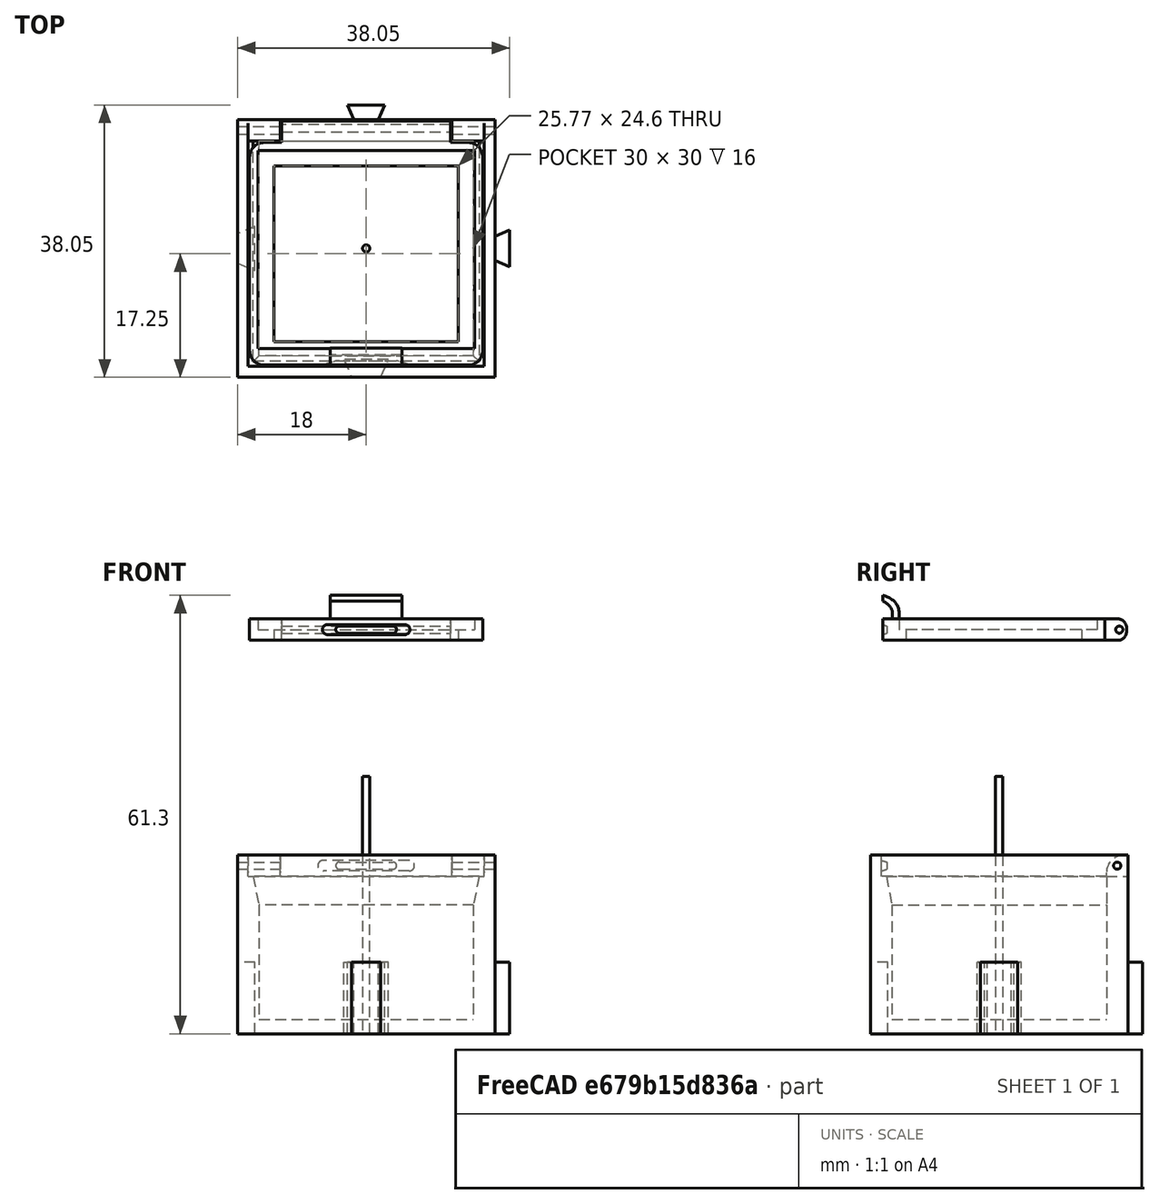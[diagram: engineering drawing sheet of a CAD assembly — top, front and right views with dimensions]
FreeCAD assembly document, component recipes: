
FREECAD ASSEMBLY — COMPONENT RECIPES ("smd_smt_modular_boxes")

This assembly document has 3 components, labeled P0..P2 below (a component is one placed body or linked part). 3 of them carry a construction recipe — the FreeCAD feature program that regenerates the part from scratch, quoted from this document or its linked companion documents; the rest are supplied as boundary geometry only. No exploded tour is included for this assembly.
COMPONENT P0 — recipe-attached ("box", modeled in this document).
Construction recipe (the document's own serialized feature program — sketch geometry with constraints, then the solid features built on it; lengths are millimeters unless a unit is written):

FEATURE [PartDesign::CoordinateSystem] LCS_0
  AttacherType = Attacher::AttachEngine3D
  MapMode = 2
  Support = -> [X_Axis001]
FEATURE [PartDesign::Plane] DatumPlane
  Length = 60
  MapMode = 5
  ResizeMode = 0
  Support = -> [XY_Plane001]
  Width = 60
FEATURE [Sketcher::SketchObject] Sketch  label="baseExternal"
  MapMode = 5
  Support = -> [DatumPlane]
  expr: Constraints[8] = Spreadsheet.lenght + Spreadsheet.wallWidth * 2
  expr: Constraints[9] = Spreadsheet.width + Spreadsheet.wallWidth * 2
  sketch-geometry (4):
    g0: LineSegment StartX=-18 StartY=18 StartZ=0 EndX=18 EndY=18 EndZ=0
    g1: LineSegment StartX=18 StartY=18 StartZ=0 EndX=18 EndY=-18 EndZ=0
    g2: LineSegment StartX=18 StartY=-18 StartZ=0 EndX=-18 EndY=-18 EndZ=0
    g3: LineSegment StartX=-18 StartY=-18 StartZ=0 EndX=-18 EndY=18 EndZ=0
  constraints (10):
    c: Coincident(g0,g1)
    c: Coincident(g1,g2)
    c: Coincident(g2,g3)
    c: Coincident(g3,g0)
    c: Horizontal(g2)
    c: Vertical(g3)
    c: Symmetric(g0,g0,g-2)
    c: Symmetric(g0,g1,g-1)
    c: DistanceX(g0,g0) = 36
    c: DistanceY(g1,g0) = 36
FEATURE [PartDesign::Pad] Pad
  Length = 22
  Length2 = 100
  Profile = -> Sketch
  Type = 0
  expr: Length = Spreadsheet.hight + Spreadsheet.buttonPad
FEATURE [PartDesign::ShapeBinder] ShapeBinder  label="baseExternalBinder"
  Support = -> [Sketch]
  TraceSupport = false
FEATURE [Sketcher::SketchObject] Sketch001  label="outsideDovetail"
  ExternalGeometry = -> [ShapeBinder]
  MapMode = 5
  Support = -> [DatumPlane]
  expr: Constraints[7] = Spreadsheet.wallWidth * 0.75 - Spreadsheet.clearance
  expr: Constraints[8] = Spreadsheet.wallWidth * 1.8 - Spreadsheet.clearance
  expr: Constraints[9] = Spreadsheet.wallWidth * 1.2 - Spreadsheet.clearance
  expr: Constraints[19] = Spreadsheet.wallWidth * 0.75 - Spreadsheet.clearance
  sketch-geometry (8):
    g0: LineSegment StartX=-1.7 StartY=18 StartZ=0 EndX=1.7 EndY=18 EndZ=0
    g1: LineSegment StartX=1.7 StartY=18 StartZ=0 EndX=2.6 EndY=20.05 EndZ=0
    g2: LineSegment StartX=2.6 StartY=20.05 StartZ=0 EndX=-2.6 EndY=20.05 EndZ=0
    g3: LineSegment StartX=-2.6 StartY=20.05 StartZ=0 EndX=-1.7 EndY=18 EndZ=0
    g4: LineSegment StartX=18 StartY=1.7 StartZ=0 EndX=18 EndY=-1.7 EndZ=0
    g5: LineSegment StartX=18 StartY=-1.7 StartZ=0 EndX=20.05 EndY=-2.6 EndZ=0
    g6: LineSegment StartX=20.05 StartY=-2.6 StartZ=0 EndX=20.05 EndY=2.6 EndZ=0
    g7: LineSegment StartX=20.05 StartY=2.6 StartZ=0 EndX=18 EndY=1.7 EndZ=0
  constraints (20):
    c: PointOnObject(g0,g-3)
    c: Coincident(g0,g1)
    c: Coincident(g1,g2)
    c: Coincident(g2,g3)
    c: Coincident(g3,g0)
    c: Symmetric(g2,g1,g-2)
    c: Symmetric(g0,g0,g-2)
    c: DistanceY(g0,g1) = 2.05
    c: DistanceX(g2,g1) = 5.2
    c: DistanceX(g0,g0) = 3.4
    c: Coincident(g4,g5)
    c: Coincident(g5,g6)
    c: Coincident(g6,g7)
    c: Coincident(g7,g4)
    c: Equal(g0,g4) = 3.8
    c: Symmetric(g4,g4,g-1)
    c: Symmetric(g5,g6,g-1)
    c: PointOnObject(g4,g-4)
    c: Equal(g2,g6)
    c: DistanceX(g4,g6) = 2.05
FEATURE [Sketcher::SketchObject] Sketch003  label="insideDovetail"
  ExternalGeometry = -> [ShapeBinder]
  MapMode = 5
  Support = -> [DatumPlane]
  expr: Constraints[19] = Spreadsheet.wallWidth * 0.75 + Spreadsheet.clearance
  expr: Constraints[7] = Spreadsheet.wallWidth * 1.3 + Spreadsheet.clearance
  expr: Constraints[6] = Spreadsheet.wallWidth * 2 + Spreadsheet.clearance
  expr: Constraints[18] = Spreadsheet.wallWidth * 0.75 + Spreadsheet.clearance
  sketch-geometry (8):
    g0: LineSegment StartX=-2.05 StartY=-18 StartZ=0 EndX=2.05 EndY=-18 EndZ=0
    g1: LineSegment StartX=2.05 StartY=-18 StartZ=0 EndX=3.1 EndY=-15.55 EndZ=0
    g2: LineSegment StartX=3.1 StartY=-15.55 StartZ=0 EndX=-3.1 EndY=-15.55 EndZ=0
    g3: LineSegment StartX=-3.1 StartY=-15.55 StartZ=0 EndX=-2.05 EndY=-18 EndZ=0
    g4: LineSegment StartX=-18 StartY=2.05 StartZ=0 EndX=-18 EndY=-2.05 EndZ=0
    g5: LineSegment StartX=-18 StartY=-2.05 StartZ=0 EndX=-15.55 EndY=-3.1 EndZ=0
    g6: LineSegment StartX=-15.55 StartY=-3.1 StartZ=0 EndX=-15.55 EndY=3.1 EndZ=0
    g7: LineSegment StartX=-15.55 StartY=3.1 StartZ=0 EndX=-18 EndY=2.05 EndZ=0
  constraints (20):
    c: Coincident(g0,g1)
    c: Coincident(g1,g2)
    c: Coincident(g2,g3)
    c: Coincident(g3,g0)
    c: Symmetric(g2,g1,g-2)
    c: Symmetric(g0,g0,g-2)
    c: DistanceX(g2,g1) = 6.2
    c: DistanceX(g0,g0) = 4.1
    c: Coincident(g4,g5)
    c: Coincident(g5,g6)
    c: Coincident(g6,g7)
    c: Coincident(g7,g4)
    c: Equal(g0,g4) = 3.8
    c: Symmetric(g4,g4,g-1)
    c: Symmetric(g5,g6,g-1)
    c: Equal(g2,g6)
    c: PointOnObject(g0,g-4)
    c: PointOnObject(g4,g-3)
    c: DistanceY(g0,g1) = 2.45
    c: DistanceX(g4,g6) = 2.45
FEATURE [PartDesign::Pad] Pad001
  BaseFeature = -> Pad
  Length = 10
  Length2 = 100
  Profile = -> Sketch001
  Type = 0
  expr: Length = Spreadsheet.hight / 2
FEATURE [PartDesign::Pocket] Pocket
  BaseFeature = -> Pad001
  Length = 10
  Length2 = 100
  Profile = -> Sketch003
  Reversed = true
  Type = 0
  expr: Length = Spreadsheet.hight / 2
FEATURE [PartDesign::Plane] DatumPlane001
  AttachmentOffset = pos=(0,0,22) rot=(0,0,1;0rad)
  Length = 60
  MapMode = 2
  Placement = pos=(0,0,22) rot=(0,0,1;0rad)
  ResizeMode = 0
  Support = -> [XY_Plane001]
  Width = 60
  expr: .AttachmentOffset.Base.z = Spreadsheet.hight + Spreadsheet.buttonPad
FEATURE [Sketcher::SketchObject] Sketch004
  MapMode = 5
  Placement = pos=(0,0,22) rot=(0,0,1;0rad)
  Support = -> [DatumPlane001]
  expr: Constraints[6] = Spreadsheet.lenght
  expr: Constraints[9] = Spreadsheet.width
  sketch-geometry (4):
    g0: LineSegment StartX=-15 StartY=15 StartZ=0 EndX=15 EndY=15 EndZ=0
    g1: LineSegment StartX=15 StartY=15 StartZ=0 EndX=15 EndY=-15 EndZ=0
    g2: LineSegment StartX=15 StartY=-15 StartZ=0 EndX=-15 EndY=-15 EndZ=0
    g3: LineSegment StartX=-15 StartY=-15 StartZ=0 EndX=-15 EndY=15 EndZ=0
  constraints (10):
    c: Coincident(g0,g1)
    c: Coincident(g1,g2)
    c: Coincident(g2,g3)
    c: Coincident(g3,g0)
    c: Horizontal(g2)
    c: Vertical(g3)
    c: DistanceX(g0,g0) = 30
    c: Symmetric(g0,g0,g-2)
    c: Symmetric(g0,g1,g-1)
    c: DistanceY(g1,g0) = 30
FEATURE [PartDesign::Pocket] Pocket001
  BaseFeature = -> Pocket
  Length = 20
  Length2 = 100
  Profile = -> Sketch004
  Type = 0
  expr: Length = Spreadsheet.hight
FEATURE [Sketcher::SketchObject] Sketch005  label="lead"
  ExternalGeometry = -> [ShapeBinder]
  MapMode = 5
  Placement = pos=(0,0,22) rot=(0,0,1;0rad)
  Support = -> [DatumPlane001]
  expr: Constraints[25] = Spreadsheet.wallWidth / 2
  expr: Constraints[23] = Spreadsheet.wallWidth
  expr: Constraints[14] = Spreadsheet.wallWidth / 2
  expr: Constraints[26] = Spreadsheet.wallWidth * 2
  sketch-geometry (12):
    g0: LineSegment StartX=-18 StartY=18 StartZ=0 EndX=-12 EndY=18 EndZ=0
    g1: LineSegment StartX=18 StartY=18 StartZ=0 EndX=18 EndY=-18 EndZ=0
    g2: LineSegment StartX=18 StartY=-18 StartZ=0 EndX=-18 EndY=-18 EndZ=0
    g3: LineSegment StartX=-18 StartY=-18 StartZ=0 EndX=-18 EndY=18 EndZ=0
    g4: LineSegment StartX=-16.5 StartY=15 StartZ=0 EndX=-12 EndY=15 EndZ=0
    g5: LineSegment StartX=16.5 StartY=15 StartZ=0 EndX=16.5 EndY=-16.5 EndZ=0
    g6: LineSegment StartX=-16.5 StartY=-16.5 StartZ=0 EndX=-16.5 EndY=15 EndZ=0
    g7: LineSegment StartX=-12 StartY=15 StartZ=0 EndX=-12 EndY=18 EndZ=0
    g8: LineSegment StartX=12 StartY=15 StartZ=0 EndX=12 EndY=18 EndZ=0
    g9: LineSegment StartX=12 StartY=15 StartZ=0 EndX=16.5 EndY=15 EndZ=0
    g10: LineSegment StartX=12 StartY=18 StartZ=0 EndX=18 EndY=18 EndZ=0
    g11: LineSegment StartX=-16.5 StartY=-16.5 StartZ=0 EndX=16.5 EndY=-16.5 EndZ=0
  constraints (30):
    c: Coincident(g10,g1)
    c: Coincident(g1,g2)
    c: Coincident(g2,g3)
    c: Coincident(g3,g0)
    c: Horizontal(g0)
    c: Horizontal(g2)
    c: Vertical(g1)
    c: Vertical(g3)
    c: Coincident(g0,g-6)
    c: Coincident(g1,g-5)
    c: Coincident(g9,g5)
    c: Coincident(g6,g4)
    c: Vertical(g6)
    c: Symmetric(g9,g4,g-2)
    c: DistanceX(g0,g4) = 1.5
    c: Vertical(g8)
    c: Parallel(g7,g-2)
    c: Coincident(g4,g7)
    c: Coincident(g9,g8)
    c: Tangent(g4,g9)
    c: Coincident(g0,g7)
    c: Coincident(g10,g8)
    c: Tangent(g0,g10)
    c: DistanceY(g4,g0) = 3
    c: Symmetric(g11,g11,g-2)
    c: DistanceY(g2,g11) = 1.5
    c: DistanceX(g0,g0) = 6
    c: Symmetric(g4,g8,g-2)
    c: Coincident(g11,g6)
    c: Coincident(g5,g11)
FEATURE [PartDesign::Pad] Pad002
  BaseFeature = -> Pocket001
  Length = 3
  Length2 = 100
  Profile = -> Sketch005
  Type = 0
  expr: Length = Spreadsheet.leadHight
FEATURE [PartDesign::Plane] DatumPlane002
  Length = 60
  MapMode = 5
  Placement = pos=(0,0,0) rot=(0.57735,0.57735,0.57735;2.0944rad)
  ResizeMode = 0
  Support = -> [YZ_Plane001]
  Width = 60
FEATURE [Sketcher::SketchObject] Sketch006  label="hingeHole"
  MapMode = 5
  Placement = pos=(0,0,0) rot=(0.57735,0.57735,0.57735;2.0944rad)
  Support = -> [DatumPlane002]
  expr: Constraints[0] = Spreadsheet.leadMountingHole / 2
  expr: Constraints[2] = Spreadsheet.hight + Spreadsheet.buttonPad + Spreadsheet.leadHight / 2
  expr: Constraints[1] = Spreadsheet.width / 2 + Spreadsheet.wallWidth * 0.5
  sketch-geometry (1):
    g0: Circle CenterX=16.5 CenterY=23.5 CenterZ=0 NormalX=0 NormalY=0 NormalZ=1 AngleXU=0 Radius=0.5
  constraints (3):
    c: Radius(g0) = 0.5
    c: DistanceX(g-1,g0) = 16.5
    c: DistanceY(g-1,g0) = 23.5
FEATURE [PartDesign::Pocket] Pocket002
  BaseFeature = -> Pad002
  Length = 5
  Length2 = 100
  Midplane = true
  Profile = -> Sketch006
  Type = 1
FEATURE [PartDesign::Plane] DatumPlane003  label="DatumPlaneLeadKeyBase"
  AttachmentOffset = pos=(0,0,16.5) rot=(0,0,1;3.14159rad)
  Length = 60
  MapMode = 5
  Placement = pos=(0,-16.5,-3.7e-15) rot=(0,-0.707107,0.707107;3.14159rad)
  ResizeMode = 0
  Support = -> [XZ_Plane001]
  Width = 60
  expr: .AttachmentOffset.Base.z = Spreadsheet.wallWidth / 2 + Spreadsheet.width / 2
FEATURE [Sketcher::SketchObject] Sketch007  label="leadKeyBase"
  MapMode = 5
  Placement = pos=(0,-16.5,-3.7e-15) rot=(0,0.707107,-0.707107;3.14159rad)
  Support = -> [DatumPlane003]
  expr: Constraints[6] = Spreadsheet.LeadKeyBaseLenght
  expr: Constraints[7] = Spreadsheet.hight + Spreadsheet.buttonPad + Spreadsheet.leadHight / 2
  expr: Constraints[8] = Spreadsheet.LeadKeyBaseWidth
  sketch-geometry (4):
    g0: ArcOfCircle CenterX=-6 CenterY=-23.5 CenterZ=0 NormalX=0 NormalY=0 NormalZ=1 AngleXU=0 Radius=0.75 StartAngle=1.5708 EndAngle=4.71239
    g1: ArcOfCircle CenterX=6 CenterY=-23.5 CenterZ=0 NormalX=0 NormalY=0 NormalZ=1 AngleXU=0 Radius=0.75 StartAngle=4.71239 EndAngle=7.85398
    g2: LineSegment StartX=-6 StartY=-24.25 StartZ=0 EndX=6 EndY=-24.25 EndZ=0
    g3: LineSegment StartX=-6 StartY=-22.75 StartZ=0 EndX=6 EndY=-22.75 EndZ=0
  constraints (9):
    c: Tangent(g0,g3)
    c: Tangent(g0,g2)
    c: Tangent(g2,g1)
    c: Tangent(g3,g1)
    c: Horizontal(g2)
    c: Symmetric(g0,g1,g-2)
    c: DistanceY(g0,g0) = 1.5
    c: DistanceY(g0,g-1) = 23.5
    c: DistanceX(g0,g1) = 12
FEATURE [PartDesign::Plane] DatumPlane004  label="DatumPlaneLeadKeyEnd"
  AttachmentOffset = pos=(0,0,15.7) rot=(0,0,1;0rad)
  Length = 60
  MapMode = 2
  Placement = pos=(0,-15.7,-3.5e-15) rot=(1,0,0;1.5708rad)
  ResizeMode = 0
  Support = -> [XZ_Plane001]
  Width = 60
  expr: .AttachmentOffset.Base.z = Spreadsheet.wallWidth / 2 + Spreadsheet.width / 2 - Spreadsheet.leadKeyPad
FEATURE [Sketcher::SketchObject] Sketch008  label="leadKeyEnd"
  ExternalGeometry = -> [Sketch007]
  MapMode = 5
  Placement = pos=(0,-15.7,-3.5e-15) rot=(1,0,0;1.5708rad)
  Support = -> [DatumPlane004]
  expr: Constraints[9] = Spreadsheet.LeadKeyEndWidth
  expr: Constraints[10] = Spreadsheet.LeadKeyEndLength
  sketch-geometry (5):
    g0: ArcOfCircle CenterX=-3.75 CenterY=23.5 CenterZ=0 NormalX=0 NormalY=0 NormalZ=1 AngleXU=0 Radius=0.5 StartAngle=1.5708 EndAngle=4.71239
    g1: ArcOfCircle CenterX=3.75 CenterY=23.5 CenterZ=0 NormalX=0 NormalY=0 NormalZ=1 AngleXU=0 Radius=0.5 StartAngle=4.71239 EndAngle=7.85398
    g2: LineSegment StartX=-3.75 StartY=23 StartZ=0 EndX=3.75 EndY=23 EndZ=0
    g3: LineSegment StartX=-3.75 StartY=24 StartZ=0 EndX=3.75 EndY=24 EndZ=0
    g4: LineSegment [constr] StartX=-6 StartY=23.5 StartZ=0 EndX=6 EndY=23.5 EndZ=0
  constraints (11):
    c: Tangent(g0,g3)
    c: Tangent(g0,g2)
    c: Tangent(g2,g1)
    c: Tangent(g3,g1)
    c: Horizontal(g2)
    c: Symmetric(g1,g0,g-2)
    c: Coincident(g4,g-3)
    c: Coincident(g4,g-4)
    c: PointOnObject(g1,g4)
    c: DistanceX(g0,g1) = 7.5
    c: DistanceY(g0,g0) = 1
FEATURE [PartDesign::AdditiveLoft] AdditiveLoft
  BaseFeature = -> Pocket002
  Closed = false
  Profile = -> Sketch007
  Ruled = false
  Sections = -> [Sketch008]
FEATURE [PartDesign::CoordinateSystem] LCS_1  label="LCDLead"
  AttacherType = Attacher::AttachEngine3D
  MapMode = 11
  Placement = pos=(-12,16.5,23.5) rot=(0.707107,0,0.707107;3.14159rad)
  Support = -> [AdditiveLoft]
FEATURE [PartDesign::CoordinateSystem] LCS_3  label="LCSPin"
  AttacherType = Attacher::AttachEngine3D
  MapMode = 11
  Placement = pos=(-13,27.25,23.5) rot=(0.707107,0,0.707107;3.14159rad)
FEATURE [PartDesign::CoordinateSystem] Local_CS
  AttacherType = Attacher::AttachEngine3D
FEATURE [PartDesign::Fillet] Fillet001
  Base = -> AdditiveLoft [Edge85,Edge89]
  BaseFeature = -> AdditiveLoft
  Radius = 2.5
  SupportTransform = false
FEATURE [PartDesign::Chamfer] Chamfer
  Angle = 45
  Base = -> Fillet001 [Edge37,Edge38,Edge39]
  BaseFeature = -> Fillet001
  ChamferType = 1
  FlipDirection = false
  Size = 0.8
  Size2 = 4
  SupportTransform = false
FEATURE [PartDesign::CoordinateSystem] LCS_4  label="LCSMale"
  AttacherType = Attacher::AttachEngine3D
  AttachmentOffset = pos=(0,0,-2.75) rot=(0,0,1;0rad)
  MapMode = 7
  Placement = pos=(20.05,0.15,-6e-16) rot=(1,0,0;1.5708rad)
  Support = -> [Chamfer]
  expr: .AttachmentOffset.Base.z = -1 * (Spreadsheet.wallWidth * 1.9 - Spreadsheet.clearance) / 2
FEATURE [PartDesign::CoordinateSystem] LCS_5  label="LCSFemale"
  AttacherType = Attacher::AttachEngine3D
  AttachmentOffset = pos=(-0.4,0,-3.1) rot=(0,0,1;0rad)
  MapMode = 7
  Placement = pos=(-15.95,0,-7e-16) rot=(1,0,0;1.5708rad)
  Support = -> [Chamfer]
  expr: .AttachmentOffset.Base.z = -1 * (Spreadsheet.wallWidth * 2 + Spreadsheet.clearance) / 2
  expr: .AttachmentOffset.Base.x = -2 * Spreadsheet.clearance
FEATURE [PartDesign::Body] box
  Group = -> [LCS_0,DatumPlane,Sketch,Pad,ShapeBinder,Sketch001,Sketch003,Pad001,Pocket,DatumPlane001,Sketch004,Pocket001,Sketch005,Pad002,DatumPlane002,Sketch006,Pocket002,DatumPlane003,Sketch007,DatumPlane004,Sketch008,AdditiveLoft,LCS_1,LCS_3,LCS_4,LCS_5,Local_CS,Fillet001,Chamfer]
  Origin = -> Origin001
  Tip = -> Chamfer
COMPONENT P1 — recipe-attached ("cover", modeled in this document).
Construction recipe (the document's own serialized feature program — sketch geometry with constraints, then the solid features built on it; lengths are millimeters unless a unit is written):

FEATURE [PartDesign::CoordinateSystem] LCS_0001
  AttacherType = Attacher::AttachEngine3D
  MapMode = 2
  Support = -> [X_Axis002]
FEATURE [PartDesign::ShapeBinder] ShapeBinder001  label="ShapeBinderLead"
  Placement = pos=(0,0,22) rot=(0,0,1;0rad)
  Support = -> [Sketch005]
  TraceSupport = false
FEATURE [Sketcher::SketchObject] Sketch009
  ExternalGeometry = -> [ShapeBinder001]
  MapMode = 5
  Support = -> [XY_Plane002]
  expr: Constraints[23] = Spreadsheet.clearance
  expr: Constraints[22] = Spreadsheet.clearance
  expr: Constraints[21] = Spreadsheet.clearance
  expr: Constraints[16] = Spreadsheet.clearance
  expr: Constraints[15] = Spreadsheet.clearance
  sketch-geometry (9):
    g0: LineSegment StartX=-11.8 StartY=14.8 StartZ=0 EndX=-16.3 EndY=14.8 EndZ=0
    g1: LineSegment StartX=-16.3 StartY=14.8 StartZ=0 EndX=-16.3 EndY=-16.3 EndZ=0
    g2: LineSegment StartX=-16.3 StartY=-16.3 StartZ=0 EndX=16.3 EndY=-16.3 EndZ=0
    g3: LineSegment StartX=16.3 StartY=-16.3 StartZ=0 EndX=16.3 EndY=14.8 EndZ=0
    g4: LineSegment StartX=16.3 StartY=14.8 StartZ=0 EndX=11.8 EndY=14.8 EndZ=0
    g5: LineSegment StartX=11.8 StartY=14.8 StartZ=0 EndX=11.8 EndY=17.8 EndZ=0
    g6: LineSegment StartX=11.8 StartY=17.8 StartZ=0 EndX=-11.8 EndY=17.8 EndZ=0
    g7: LineSegment StartX=-11.8 StartY=17.8 StartZ=0 EndX=-11.8 EndY=14.8 EndZ=0
    g8: LineSegment [constr] StartX=-11.8 StartY=14.8 StartZ=0 EndX=11.8 EndY=14.8 EndZ=0
  constraints (24):
    c: Coincident(g7,g6)
    c: Coincident(g0,g7)
    c: Coincident(g1,g0)
    c: Coincident(g1,g2)
    c: Coincident(g3,g2)
    c: Coincident(g6,g5)
    c: Coincident(g4,g5)
    c: Coincident(g4,g3)
    c: Parallel(g-1,g0)
    c: Parallel(g-1,g4)
    c: Parallel(g-1,g2)
    c: Parallel(g-2,g3)
    c: Parallel(g-2,g1)
    c: Parallel(g-2,g5)
    c: Parallel(g-2,g7)
    c: DistanceY(g6,g-11) = 0.2
    c: DistanceY(g0,g-11) = 0.2
    c: Coincident(g8,g0)
    c: Coincident(g8,g4)
    c: Symmetric(g6,g5,g-2)
    c: Symmetric(g0,g3,g-2)
    c: DistanceX(g-9,g0) = 0.2
    c: DistanceX(g-11,g6) = 0.2
    c: DistanceY(g-7,g1) = 0.2
FEATURE [PartDesign::Pad] Pad003
  Length = 3
  Length2 = 100
  Profile = -> Sketch009
  Type = 0
  expr: Length = Spreadsheet.leadHight
FEATURE [PartDesign::Plane] DatumPlane005  label="DatumPlaneleadKeyOutside"
  AttachmentOffset = pos=(0,0,16.5) rot=(0,0,1;0rad)
  Length = 60
  MapMode = 5
  Placement = pos=(0,-16.5,-3.7e-15) rot=(1,0,0;1.5708rad)
  ResizeMode = 0
  Support = -> [XZ_Plane002]
  Width = 60
  expr: .AttachmentOffset.Base.z = Spreadsheet.width / 2 + Spreadsheet.wallWidth / 2
FEATURE [Sketcher::SketchObject] Sketch010  label="leadKeyOutside"
  MapMode = 5
  Placement = pos=(0,-16.5,-3.7e-15) rot=(1,0,0;1.5708rad)
  Support = -> [DatumPlane005]
  expr: Constraints[6] = Spreadsheet.LeadKeyBaseWidth
  expr: Constraints[7] = Spreadsheet.LeadKeyBaseLenght
  expr: Constraints[8] = Spreadsheet.leadHight / 2
  sketch-geometry (4):
    g0: ArcOfCircle CenterX=-6 CenterY=1.5 CenterZ=0 NormalX=0 NormalY=0 NormalZ=1 AngleXU=0 Radius=0.75 StartAngle=1.5708 EndAngle=4.71239
    g1: ArcOfCircle CenterX=6 CenterY=1.5 CenterZ=0 NormalX=0 NormalY=0 NormalZ=1 AngleXU=0 Radius=0.75 StartAngle=4.71239 EndAngle=7.85398
    g2: LineSegment StartX=-6 StartY=0.75 StartZ=0 EndX=6 EndY=0.75 EndZ=0
    g3: LineSegment StartX=-6 StartY=2.25 StartZ=0 EndX=6 EndY=2.25 EndZ=0
  constraints (9):
    c: Tangent(g0,g3)
    c: Tangent(g0,g2)
    c: Tangent(g2,g1)
    c: Tangent(g3,g1)
    c: Horizontal(g2)
    c: Symmetric(g0,g1,g-2)
    c: DistanceX(g0,g1) = 12
    c: DistanceY(g0,g0) = 1.5
    c: DistanceY(g-1,g0) = 1.5
FEATURE [PartDesign::Plane] DatumPlane006
  AttachmentOffset = pos=(0,0,15.7) rot=(0,0,1;0rad)
  Length = 60
  MapMode = 5
  Placement = pos=(0,-15.7,-3.5e-15) rot=(1,0,0;1.5708rad)
  ResizeMode = 0
  Support = -> [XZ_Plane002]
  Width = 60
  expr: .AttachmentOffset.Base.z = Spreadsheet.width / 2 + Spreadsheet.wallWidth / 2 - Spreadsheet.leadKeyPad
FEATURE [Sketcher::SketchObject] Sketch011  label="leadKeyInside"
  MapMode = 5
  Placement = pos=(0,-15.7,-3.5e-15) rot=(1,0,0;1.5708rad)
  Support = -> [DatumPlane006]
  expr: Constraints[6] = Spreadsheet.leadHight / 2
  expr: Constraints[7] = Spreadsheet.LeadKeyEndLength
  expr: Constraints[8] = Spreadsheet.LeadKeyEndWidth
  sketch-geometry (4):
    g0: ArcOfCircle CenterX=-3.75 CenterY=1.5 CenterZ=0 NormalX=0 NormalY=0 NormalZ=1 AngleXU=0 Radius=0.5 StartAngle=1.5708 EndAngle=4.71239
    g1: ArcOfCircle CenterX=3.75 CenterY=1.5 CenterZ=0 NormalX=0 NormalY=0 NormalZ=1 AngleXU=0 Radius=0.5 StartAngle=4.71239 EndAngle=7.85398
    g2: LineSegment StartX=-3.75 StartY=1 StartZ=0 EndX=3.75 EndY=1 EndZ=0
    g3: LineSegment StartX=-3.75 StartY=2 StartZ=0 EndX=3.75 EndY=2 EndZ=0
  constraints (9):
    c: Tangent(g0,g3)
    c: Tangent(g0,g2)
    c: Tangent(g2,g1)
    c: Tangent(g3,g1)
    c: Horizontal(g2)
    c: Symmetric(g0,g1,g-2)
    c: DistanceY(g-1,g0) = 1.5
    c: DistanceY(g0,g0) = 1
    c: DistanceX(g0,g1) = 7.5
FEATURE [PartDesign::SubtractiveLoft] SubtractiveLoft
  BaseFeature = -> Pad003
  Closed = false
  Profile = -> Sketch010
  Ruled = false
  Sections = -> [Sketch011]
FEATURE [PartDesign::Plane] DatumPlane007
  Length = 60
  MapMode = 5
  Placement = pos=(0,0,0) rot=(0.57735,0.57735,0.57735;2.0944rad)
  ResizeMode = 0
  Support = -> [YZ_Plane002]
  Width = 60
FEATURE [Sketcher::SketchObject] Sketch012  label="hingleHole"
  MapMode = 5
  Placement = pos=(0,0,0) rot=(0.57735,0.57735,0.57735;2.0944rad)
  Support = -> [DatumPlane007]
  expr: Constraints[0] = Spreadsheet.width / 2 + Spreadsheet.wallWidth * 0.6
  expr: Constraints[1] = Spreadsheet.leadHight / 2
  expr: Constraints[2] = Spreadsheet.leadMountingHole / 2
  sketch-geometry (1):
    g0: Circle CenterX=16.8 CenterY=1.5 CenterZ=0 NormalX=0 NormalY=0 NormalZ=1 AngleXU=0 Radius=0.5
  constraints (3):
    c: DistanceX(g-1,g0) = 16.8
    c: DistanceY(g-1,g0) = 1.5
    c: Radius(g0) = 0.5
FEATURE [PartDesign::Pocket] Pocket003
  BaseFeature = -> SubtractiveLoft
  Length = 5
  Length2 = 100
  Midplane = true
  Profile = -> Sketch012
  Type = 1
FEATURE [PartDesign::Plane] DatumPlane008
  AttachmentOffset = pos=(0,0,3) rot=(0,0,1;0rad)
  Length = 60
  MapMode = 5
  Placement = pos=(0,0,3) rot=(0,0,1;0rad)
  ResizeMode = 0
  Support = -> [XY_Plane002]
  Width = 60
  expr: .AttachmentOffset.Base.z = Spreadsheet.leadHight
FEATURE [Sketcher::SketchObject] Sketch013  label="resessForCover"
  ExternalGeometry = -> [ShapeBinder001]
  MapMode = 5
  Placement = pos=(0,0,3) rot=(0,0,1;0rad)
  Support = -> [DatumPlane008]
  sketch-geometry (6):
    g0: LineSegment StartX=-15.1381 StartY=13.7 StartZ=0 EndX=15.1381 EndY=13.7 EndZ=0
    g1: LineSegment StartX=15.1381 StartY=13.7 StartZ=0 EndX=15.1381 EndY=-14 EndZ=0
    g2: LineSegment StartX=15.1381 StartY=-14 StartZ=0 EndX=-15.1381 EndY=-14 EndZ=0
    g3: LineSegment StartX=-15.1381 StartY=-14 StartZ=0 EndX=-15.1381 EndY=13.7 EndZ=0
    g4: LineSegment [constr] StartX=-16.5 StartY=-16.5 StartZ=0 EndX=16.5 EndY=15 EndZ=0
    g5: LineSegment [constr] StartX=-16.5 StartY=15 StartZ=0 EndX=16.5 EndY=-16.5 EndZ=0
  constraints (16):
    c: Coincident(g0,g1)
    c: Coincident(g1,g2)
    c: Coincident(g2,g3)
    c: Coincident(g3,g0)
    c: Horizontal(g0)
    c: Horizontal(g2)
    c: Vertical(g1)
    c: Vertical(g3)
    c: Coincident(g-5,g4)
    c: Coincident(g5,g-7)
    c: Coincident(g5,g-4)
    c: PointOnObject(g0,g5)
    c: PointOnObject(g0,g4)
    c: Coincident(g4,g-7)
    c: DistanceY(g0,g5) = 1.3
    c: DistanceY(g4,g2) = 2.5
FEATURE [Sketcher::SketchObject] Sketch014  label="centralCut"
  ExternalGeometry = -> [ShapeBinder001]
  MapMode = 5
  Placement = pos=(0,0,3) rot=(0,0,1;0rad)
  Support = -> [DatumPlane008]
  sketch-geometry (6):
    g0: LineSegment [constr] StartX=-16.5 StartY=15 StartZ=0 EndX=16.5 EndY=-16.5 EndZ=0
    g1: LineSegment [constr] StartX=16.5 StartY=15 StartZ=0 EndX=-16.5 EndY=-16.5 EndZ=0
    g2: LineSegment StartX=-12.8832 StartY=11.5476 StartZ=0 EndX=12.8832 EndY=11.5476 EndZ=0
    g3: LineSegment StartX=12.8832 StartY=11.5476 StartZ=0 EndX=12.8832 EndY=-13.0476 EndZ=0
    g4: LineSegment StartX=12.8832 StartY=-13.0476 StartZ=0 EndX=-12.8832 EndY=-13.0476 EndZ=0
    g5: LineSegment StartX=-12.8832 StartY=-13.0476 StartZ=0 EndX=-12.8832 EndY=11.5476 EndZ=0
  constraints (16):
    c: Coincident(g0,g-4)
    c: Coincident(g0,g-6)
    c: Coincident(g1,g-7)
    c: Coincident(g1,g-5)
    c: Coincident(g2,g3)
    c: Coincident(g3,g4)
    c: Coincident(g4,g5)
    c: Coincident(g5,g2)
    c: Horizontal(g2)
    c: Horizontal(g4)
    c: Vertical(g3)
    c: Vertical(g5)
    c: PointOnObject(g2,g0)
    c: PointOnObject(g3,g0)
    c: PointOnObject(g2,g1)
    c: Distance(g2,g0) = 5
FEATURE [PartDesign::Pocket] Pocket004
  BaseFeature = -> Pocket003
  Length = 1.5
  Length2 = 100
  Profile = -> Sketch013
  Type = 0
  expr: Length = Spreadsheet.leadHight / 2
FEATURE [PartDesign::Pocket] Pocket005
  BaseFeature = -> Pocket004
  Length = 5
  Length2 = 100
  Profile = -> Sketch014
  Type = 1
FEATURE [PartDesign::CoordinateSystem] LCS_2
  AttacherType = Attacher::AttachEngine3D
  MapMode = 11
  Placement = pos=(-11.8,16.8,1.5) rot=(0.707107,0,0.707107;3.14159rad)
  Support = -> [Pocket005]
  expr: .AttachmentOffset.Rotation.Yaw = Variables.angleLead
  expr: .AttachmentOffset.Base.x = 0mm
FEATURE [PartDesign::Fillet] Fillet
  Base = -> Pocket005 [Edge21,Edge12]
  BaseFeature = -> Pocket005
  Radius = 1.2
  SupportTransform = false
FEATURE [PartDesign::Plane] DatumPlane009  label="DatumPlanehandle"
  Length = 60
  MapMode = 5
  Placement = pos=(0,0,0) rot=(0.57735,0.57735,0.57735;2.0944rad)
  ResizeMode = 0
  Support = -> [YZ_Plane002]
  Width = 60
FEATURE [Sketcher::SketchObject] Sketch018  label="handle"
  ExternalGeometry = -> [Sketch009,Sketch013]
  MapMode = 5
  Placement = pos=(0,0,0) rot=(0.57735,0.57735,0.57735;2.0944rad)
  Support = -> [DatumPlane009]
  sketch-geometry (17):
    g0: LineSegment [constr] StartX=-16.3 StartY=-1.8e-15 StartZ=0 EndX=-16.3 EndY=13.596 EndZ=0
    g1: LineSegment StartX=-14 StartY=3 StartZ=0 EndX=-15 EndY=3 EndZ=0
    g2: Circle [constr] CenterX=-14 CenterY=3 CenterZ=0 NormalX=0 NormalY=0 NormalZ=1 AngleXU=0 Radius=0.3
    g3: Circle [constr] CenterX=-13.6798 CenterY=5.61911 CenterZ=0 NormalX=0 NormalY=0 NormalZ=1 AngleXU=0 Radius=0.3
    g4: Circle [constr] CenterX=-16.3 CenterY=6.3 CenterZ=0 NormalX=0 NormalY=0 NormalZ=1 AngleXU=0 Radius=0.3
    g5: BSplineCurve PolesCount=3 KnotsCount=2 Degree=2 IsPeriodic=0
    g6: GeomPoint [constr] X=-14 Y=3 Z=0
    g7: GeomPoint [constr] X=-16.3 Y=6.3 Z=0
    g8: Circle [constr] CenterX=-15 CenterY=3 CenterZ=0 NormalX=0 NormalY=0 NormalZ=1 AngleXU=0 Radius=0.2
    g9: Circle [constr] CenterX=-14.5899 CenterY=4.69846 CenterZ=0 NormalX=0 NormalY=0 NormalZ=1 AngleXU=0 Radius=0.2
    g10: Circle [constr] CenterX=-16.3 CenterY=5.5 CenterZ=0 NormalX=0 NormalY=0 NormalZ=1 AngleXU=0 Radius=0.2
    g11: BSplineCurve PolesCount=3 KnotsCount=2 Degree=2 IsPeriodic=0
    g12: GeomPoint [constr] X=-15 Y=3 Z=0
    g13: GeomPoint [constr] X=-16.3 Y=5.5 Z=0
    g14: LineSegment StartX=-16.3 StartY=5.5 StartZ=0 EndX=-16.3 EndY=6.3 EndZ=0
    g15: LineSegment [constr] StartX=-16.3 StartY=-1.8e-15 StartZ=0 EndX=-14.5899 EndY=4.69846 EndZ=0
    g16: LineSegment [constr] StartX=-16.3 StartY=-1.8e-15 StartZ=0 EndX=-13.6798 EndY=5.61911 EndZ=0
  constraints (37):
    c: Coincident(g0,g-3)
    c: Vertical(g0)
    c: Parallel(g1,g-1)
    c: Coincident(g5,g1)
    c: Radius(g2) = 0.3
    c: Equal(g2,g3)
    c: Equal(g2,g4)
    c: PointOnObject(g5,g0)
    c: InternalAlignment(g2,g5)
    c: InternalAlignment(g3,g5)
    c: InternalAlignment(g4,g5)
    c: InternalAlignment(g6,g5)
    c: InternalAlignment(g7,g5)
    c: Coincident(g11,g1)
    c: Radius(g8) = 0.2
    c: Equal(g8,g9)
    c: Equal(g8,g10)
    c: PointOnObject(g11,g0)
    c: InternalAlignment(g8,g11)
    c: InternalAlignment(g9,g11)
    c: InternalAlignment(g10,g11)
    c: InternalAlignment(g12,g11)
    c: InternalAlignment(g13,g11)
    c: Coincident(g14,g11)
    c: Coincident(g14,g5)
    c: DistanceY(g11,g5) = 0.8
    c: Coincident(g1,g-4)
    c: DistanceX(g1,g1) = 1
    c: DistanceY(g1,g11) = 2.5
    c: Coincident(g15,g0)
    c: Coincident(g15,g9)
    c: Coincident(g16,g0)
    c: Coincident(g16,g3)
    c: Angle(g-1,g16) = 1.13446
    c: Angle(g-1,g15) = 1.22173
    c: Distance(g0,g9) = 5
    c: Distance(g0,g3) = 6.2
FEATURE [PartDesign::Pad] Pad005
  BaseFeature = -> Fillet
  Length = 10
  Length2 = 100
  Midplane = true
  Profile = -> Sketch018
  Type = 0
FEATURE [PartDesign::Fillet] Fillet002
  Base = -> Pad005 [Edge45,Edge44,Edge39,Edge43]
  BaseFeature = -> Pad005
  Radius = 2
  SupportTransform = false
FEATURE [PartDesign::Body] cover
  Group = -> [LCS_0001,ShapeBinder001,Sketch009,Pad003,DatumPlane005,Sketch010,DatumPlane006,Sketch011,SubtractiveLoft,DatumPlane007,Sketch012,Pocket003,DatumPlane008,Sketch013,Sketch014,Pocket004,Pocket005,LCS_2,Fillet,DatumPlane009,Sketch018,Pad005,Fillet002]
  Origin = -> Origin002
  Placement = pos=(0,0,55) rot=(0,0,1;0rad)
  Tip = -> Fillet002
COMPONENT P2 — recipe-attached ("hingePin", modeled in this document).
Construction recipe (the document's own serialized feature program — sketch geometry with constraints, then the solid features built on it; lengths are millimeters unless a unit is written):

FEATURE [PartDesign::CoordinateSystem] LCS_0002  label="LCSHingePin"
  AttacherType = Attacher::AttachEngine3D
  MapMode = 2
  Support = -> [X_Axis003]
FEATURE [Sketcher::SketchObject] Sketch015
  MapMode = 5
  Support = -> [XY_Plane003]
  expr: Constraints[1] = Spreadsheet.leadMountingHole / 2
  sketch-geometry (1):
    g0: Circle CenterX=0 CenterY=0 CenterZ=0 NormalX=0 NormalY=0 NormalZ=1 AngleXU=0 Radius=0.5
  constraints (2):
    c: Coincident(g0,g-1)
    c: Radius(g0) = 0.5
FEATURE [PartDesign::Pad] Pad004
  Length = 36
  Length2 = 100
  Profile = -> Sketch015
  Type = 0
  expr: Length = Spreadsheet.lenght + Spreadsheet.wallWidth * 2
FEATURE [PartDesign::Body] hingePin
  Group = -> [LCS_0002,Sketch015,Pad004]
  Origin = -> Origin003
  Tip = -> Pad004
PROVENANCE & LICENSES
A FreeCAD (.FCStd) document from a public repository crawl; recipes are the document's own serialized feature recipes (and, for linked parts, companion documents' recipes).
License: as declared in the source repository (recorded in the dataset sidecar).
